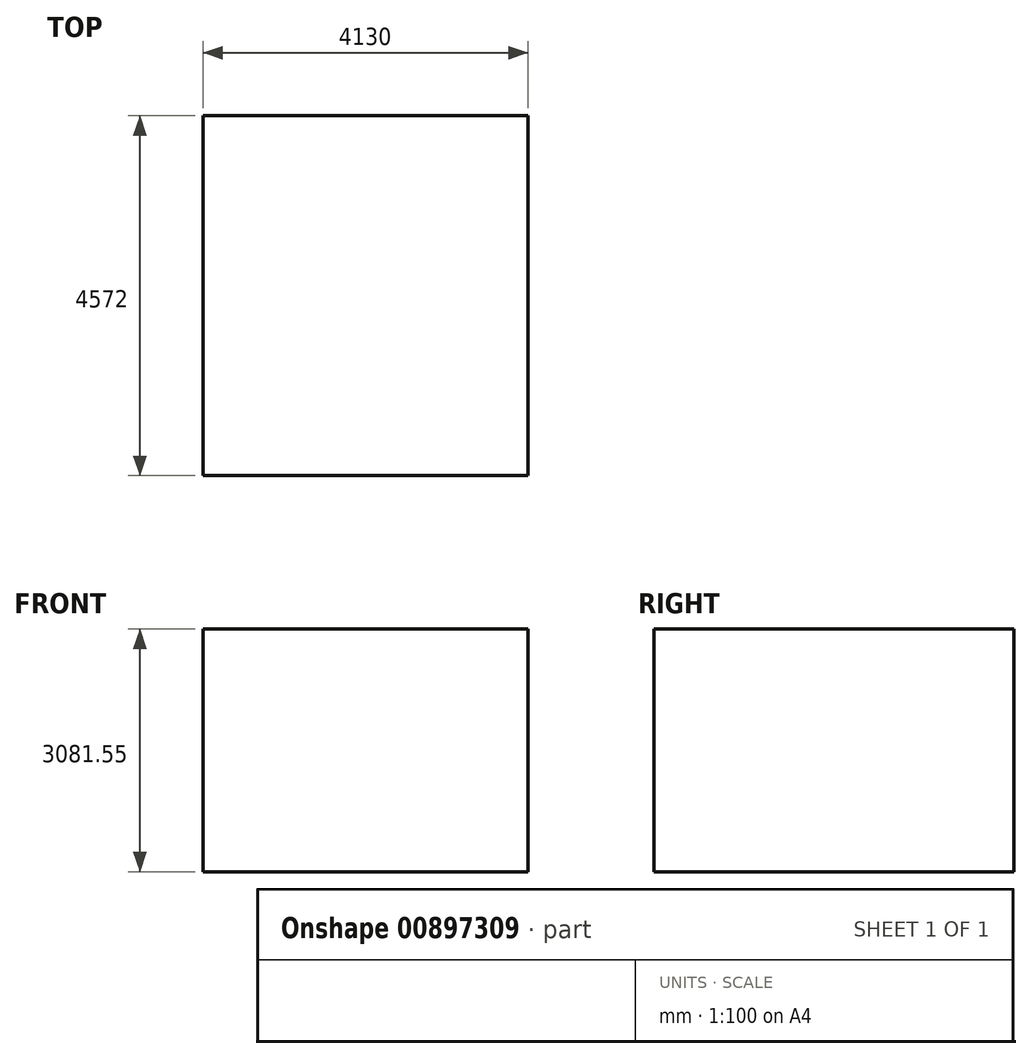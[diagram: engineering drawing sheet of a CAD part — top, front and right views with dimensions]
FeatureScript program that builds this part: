
annotation { "Feature Type Name" : "Feature", "Feature Type Description" : "" }
export const myFeature = defineFeature(function(context is Context, id is Id, definition is map)
    precondition{}
    {
        {
            var Q0;
            Q0=qCreatedBy(makeId("Front.planeOp"),FACE);
            var sketch = newSketch(context, id + "F0", { "sketchPlane" : qUnion([Q0])});
            skLineSegment(sketch, "E0.bottom", {"start": v(0, 0) * mm, "end": v(4130, 0) * mm});
            skLineSegment(sketch, "E0.top", {"start": v(0, 3081.55) * mm, "end": v(4130, 3081.55) * mm});
            skLineSegment(sketch, "E0.left", {"start": v(0, 0) * mm, "end": v(0, 3081.55) * mm});
            skLineSegment(sketch, "E0.right", {"start": v(4130, 0) * mm, "end": v(4130, 3081.55) * mm});
            skSolve(sketch);
        }
        {
            var Q0;
            Q0=makeQuery(id+"F0.imprint","IMPRINT",FACE,{"disambiguationData":[TD([[makeQuery(id+"F0.imprint","IMPRINT",EDGE,{"derivedFrom":sQuery(id+"F0.wireOp",EDGE,"E0.bottom")}),1.0]])]});
            extrude(context, id + "F1", {"entities" : qUnion([Q0]), "oppositeDirection" : true, "depth" : 4572 * mm, "offsetDistance" : 25.4 * mm});
        }
    });
